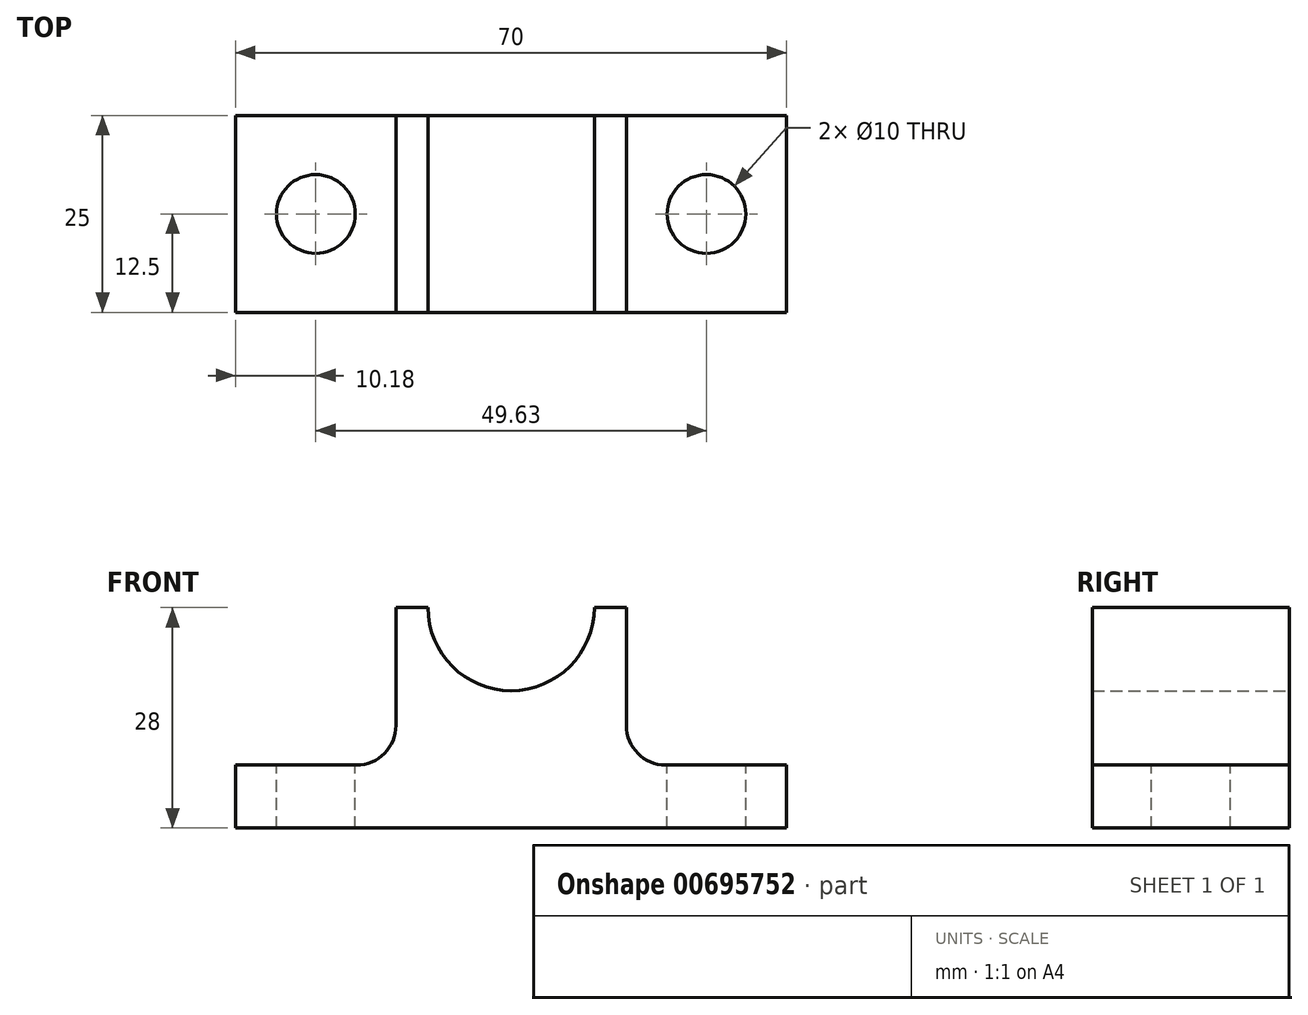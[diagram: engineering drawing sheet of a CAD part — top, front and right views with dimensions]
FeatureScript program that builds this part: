
annotation { "Feature Type Name" : "Feature", "Feature Type Description" : "" }
export const myFeature = defineFeature(function(context is Context, id is Id, definition is map)
    precondition{}
    {
        {
            var Q0;
            Q0=qCreatedBy(makeId("Front.planeOp"),FACE);
            var sketch = newSketch(context, id + "F0", { "sketchPlane" : qUnion([Q0])});
            skLineSegment(sketch, "E0", {"start": v(-29.81, 0) * mm, "end": v(40.19, 0) * mm});
            skLineSegment(sketch, "E1", {"start": v(40.19, 0) * mm, "end": v(40.19, 8) * mm});
            skLineSegment(sketch, "E2", {"start": v(40.19, 8) * mm, "end": v(19.81, 8) * mm});
            skLineSegment(sketch, "E3", {"start": v(19.81, 8) * mm, "end": v(19.81, 28) * mm});
            skLineSegment(sketch, "E4", {"start": v(19.81, 28) * mm, "end": v(15.75, 28) * mm});
            skLineSegment(sketch, "E5", {"start": v(-9.44, 28) * mm, "end": v(-9.44, 8) * mm});
            skLineSegment(sketch, "E6", {"start": v(-9.44, 8) * mm, "end": v(-29.81, 8) * mm});
            skLineSegment(sketch, "E7", {"start": v(-29.81, 8) * mm, "end": v(-29.81, 0) * mm});
            skArc(sketch, "E8", {"start": v(-5.38, 28) * mm, "mid": v(5.19, 17.44) * mm, "end": v(15.75, 28) * mm});
            skLineSegment(sketch, "E9.trimOffspring", {"start": v(-5.38, 28) * mm, "end": v(-9.44, 28) * mm});
            skSolve(sketch);
        }
        {
            var Q0;
            Q0 = qSketchRegion(id + "F0", true);
            extrude(context, id + "F1", {"entities" : qUnion([Q0]), "depth" : 25 * mm, "offsetDistance" : 25 * mm});
        }
        {
            var Q0;
            Q0=makeQuery(id+"F1.opExtrude","SWEPT_FACE",FACE,{"disambiguationData":[OSD([sQuery(id+"F0.wireOp",EDGE,"E6")])]});
            var sketch = newSketch(context, id + "F2", { "sketchPlane" : qUnion([Q0])});
            skLineSegment(sketch, "E10.0.0", {"start": v(40.19, 0) * mm, "end": v(19.81, 0) * mm});
            skLineSegment(sketch, "E10.0.1", {"start": v(19.81, 0) * mm, "end": v(19.81, -25) * mm});
            skLineSegment(sketch, "E10.0.2", {"start": v(19.81, -25) * mm, "end": v(40.19, -25) * mm});
            skLineSegment(sketch, "E10.0.3", {"start": v(40.19, -25) * mm, "end": v(40.19, 0) * mm});
            skPoint(sketch, "E11", {"position": v(-19.63, -12.5) * mm});
            skPoint(sketch, "E11.positionSnap0", {"position": v(-29.81, -12.5) * mm});
            skPoint(sketch, "E11.positionSnap1", {"position": v(-19.63, 0) * mm});
            skPoint(sketch, "E12", {"position": v(30, -12.5) * mm});
            skPoint(sketch, "E12.positionSnap0", {"position": v(40.19, -12.5) * mm});
            skPoint(sketch, "E12.positionSnap1", {"position": v(30, 0) * mm});
            skSolve(sketch);
        }
        {
            var Q0;
            Q0=sQuery(id+"F2.wireOp",VERTEX,"E11");
            var Q1;
            Q1=makeQuery(id+"F1.opExtrude","SWEPT_BODY",BODY,{"disambiguationData":[OSD([sQuery(id+"F0.wireOp",EDGE,"E0"),sQuery(id+"F0.wireOp",EDGE,"E1"),sQuery(id+"F0.wireOp",EDGE,"E2"),sQuery(id+"F0.wireOp",EDGE,"E3"),sQuery(id+"F0.wireOp",EDGE,"E4"),sQuery(id+"F0.wireOp",EDGE,"E5"),sQuery(id+"F0.wireOp",EDGE,"E6"),sQuery(id+"F0.wireOp",EDGE,"E7"),sQuery(id+"F0.wireOp",EDGE,"E8"),sQuery(id+"F0.wireOp",EDGE,"E9.trimOffspring")])]});
            hole(context, id + "F3", {"style" : HoleStyle.SIMPLE, "endStyle" : HoleEndStyle.THROUGH, "holeDiameter" : 10 * mm, "majorDiameter" : 5 * mm, "isTappedThrough" : true, "tappedDepth" : 12 * mm, "tapClearance" : 3, "locations" : qUnion([Q0]), "scope" : qUnion([Q1])});
        }
        {
            var Q0;
            Q0=sQuery(id+"F2.wireOp",VERTEX,"E12");
            var Q1;
            Q1=makeQuery(id+"F1.opExtrude","SWEPT_BODY",BODY,{"disambiguationData":[OSD([sQuery(id+"F0.wireOp",EDGE,"E0"),sQuery(id+"F0.wireOp",EDGE,"E1"),sQuery(id+"F0.wireOp",EDGE,"E2"),sQuery(id+"F0.wireOp",EDGE,"E3"),sQuery(id+"F0.wireOp",EDGE,"E4"),sQuery(id+"F0.wireOp",EDGE,"E5"),sQuery(id+"F0.wireOp",EDGE,"E6"),sQuery(id+"F0.wireOp",EDGE,"E7"),sQuery(id+"F0.wireOp",EDGE,"E8"),sQuery(id+"F0.wireOp",EDGE,"E9.trimOffspring")])]});
            hole(context, id + "F4", {"style" : HoleStyle.SIMPLE, "endStyle" : HoleEndStyle.THROUGH, "holeDiameter" : 10 * mm, "majorDiameter" : 5 * mm, "isTappedThrough" : true, "tappedDepth" : 12 * mm, "tapClearance" : 3, "locations" : qUnion([Q0]), "scope" : qUnion([Q1])});
        }
        {
            var Q0;
            Q0=makeQuery(id+"F1.opExtrude","SWEPT_EDGE",EDGE,{"disambiguationData":[OSD([sQuery(id+"F0.wireOp",EDGE,"E5"),sQuery(id+"F0.wireOp",EDGE,"E6")])]});
            var Q1;
            Q1=makeQuery(id+"F1.opExtrude","SWEPT_EDGE",EDGE,{"disambiguationData":[OSD([sQuery(id+"F0.wireOp",EDGE,"E2"),sQuery(id+"F0.wireOp",EDGE,"E3")])]});
            fillet(context, id + "F5", {"entities" : qUnion([Q0, Q1]), "radius" : 5 * mm, "tangentPropagation" : true, "allowEdgeOverflow" : false});
        }
    });
